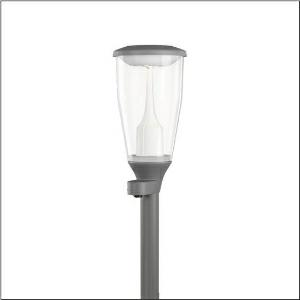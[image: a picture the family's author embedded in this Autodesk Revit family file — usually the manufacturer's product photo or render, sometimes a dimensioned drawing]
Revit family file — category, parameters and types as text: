
# Revit family: dl_11_iq___st1_2a_5xa5565eu14h000022_1a9b
name_source: partatom
category: Lighting Fixtures
units: mm (PartAtom-declared; Revit-internal decimal feet)

## family parameters
Cut with Voids When Loaded = No
Host = Face
Light Source = No
Part Type = Normal
Room Calculation Point = No
Round Connector Dimension = Use Diameter
Shared = No

## types (1)
- --- (1 x LED, 1560 lm, 10.7 W, 3000K)
    Apparent Load = 11 VA
    CIE Flux Codes = 24 63 94 96 100
    Color Rendering = 70
    Color Temperature = 3000K
    Default Elevation = 1800 mm
    Description = DL 11 iQ, mast luminaire, Module 540 iQ-SR, primary light control with 3 zone facetted reflector, of plastic, silver coated, highly specular, structured, primary optical cover: cover, of PMMA, transparent, light distribution: ST1.2a, light emission: direct distribution, primary light characteristic: asymmetric, installation type: post-top, LED, High Power LED, rated luminous flux: 1.560lm, luminous efficacy: 146lm/W, light colour: 730, colour temperature: 3000K, control gear: iQ-Street Remote, D4i with power reduction, control: pre-setting: logarithmic dimming characteristic, Street-Remote, Auto-Match, Temp-Guard, Lumen-Switch, Night-Set, Smart-Wire, Light-Fading, Desk-Remote (wireless, voltage-free reading and setting of iQ features in the workshop via application-optimized NFC function/RFID function), optimised constant luminous flux control (CLO 2.0), mains connection: 220..240V, AC, 50/60Hz, connection cable pre-assembled, cable length: 5,5m, start of lifetime: 11W, end of service life: 11W, reduction: 6W, luminaire housing, upper part, of diecast aluminium, coated, SITECO metallic grey (DB 702S), spigot size: 60mm (post-top), mounting height: 3..5m, post-top mast mounting element, of diecast aluminium, coated, SITECO metallic grey (DB 702S), Module 540 iQ-SR, traffic white (RAL 9016), equipment: standard, Smart Interface below, protection rating (complete): IP66, insulation class (complete): insulation class II (safety insulation), certification: CE, ENEC, ENEC+, VDE, impact resistance: IK07, packaging unit: 1 piece

Light Distribution: ST1.2a
    Height = 665 mm
    Lamp = 1 x LED
    Lamp Light Flux = 1560 lm
    Lamp Power = 10.7 W
    Lamp count = 1
    Length = 334 mm
    Luminous efficacy = 146 lm/W
    Manufacturer = Siteco
    ModVariant = No
    Model = 5XA5565EU14H000022
    Number of Poles = 1
    OnlyDefault = Yes
    Power Factor = 1
    Product Name = DL 11 iQ | ST1.2a
    Product group = mast luminaire | pylon top
    ProductGroupID = 6100
    Protection Class = Protection class II
    Protection Degree = IP 66
    RLX_Detail_Level = 1
    RLX_Emergency_Light_Flux = 0 lm
    RLX_Emergency_Type = 0
    RLX_Emergency_Type_DB = No
    RlxData = <blob elided: 159293 chars, md5=5cb04f42>
    Socket = socket
    Standby Power = 0 W
    System Light Flux = 1560 lm
    System Power = 11 W
    Type Comments = factory setting: luminous flux: 100 % | dim-lin: 254 | 419 mA
    Type Image = l_1337539.jpg
    URL = http://relux.com
    VarID = @adj_098997
    Voltage = 0 V
    Weight = 0.00 kg
    Width = 0 mm  [stored 0 ft]

note: [stored X ft] marks values corroborated as IEEE doubles in the binary element streams (Revit-internal decimal feet)

## geometry (parser evidence)
native form markers: Blend x4, Sweep x10
no freeform markers — native parametric forms only
